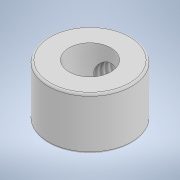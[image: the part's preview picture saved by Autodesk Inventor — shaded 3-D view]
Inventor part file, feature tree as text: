
AUTODESK INVENTOR PART (.ipt)
format: ipt  version: 2022 (Build 260153000, 153)  size: 139,264 bytes
history: native  units: mm
features: sketch x3, extrude x2, fillet x2, other x1, hole x1
ambient origin geometry x8: Origin, YZ Plane, XZ Plane, XY Plane, X Axis, Y Axis, Z Axis, Center Point
bodies: Body1 (feature_tree)
feature tree (9):
  other  "ソリッド1"
  extrude  "押し出し1"  Depth=8.0mm
  fillet  "フィレット1"  Radius=5.0mm
  fillet  "フィレット2"  Radius=0.2mm
  extrude  "押し出し2"  Depth=0.2mm
  hole  "穴1"  [1 undecoded]
  sketch  "スケッチ1"
  sketch  "スケッチ2"
  sketch  "スケッチ3"
note: 1 required parameter value undecoded (feature->parameter linkage not recoverable at this tier; creation-order binding heuristic only, values carry confidence <= 0.55)
